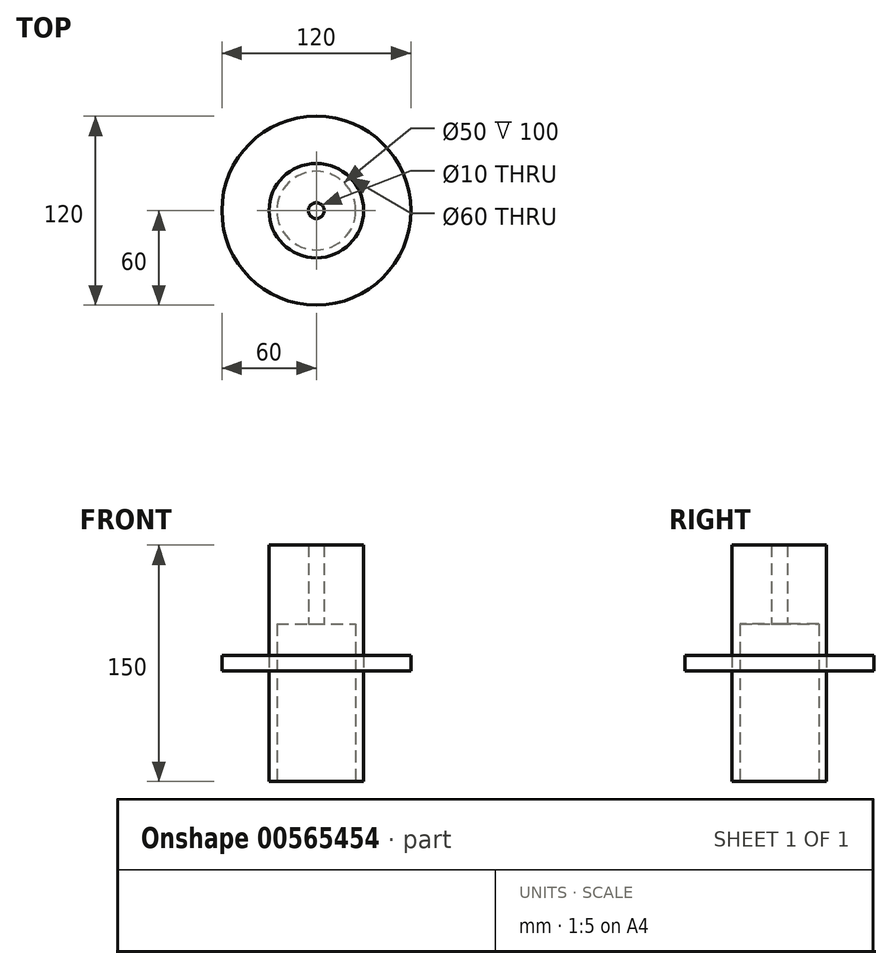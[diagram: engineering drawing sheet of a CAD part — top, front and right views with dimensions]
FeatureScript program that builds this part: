
annotation { "Feature Type Name" : "Feature", "Feature Type Description" : "" }
export const myFeature = defineFeature(function(context is Context, id is Id, definition is map)
    precondition{}
    {
        {
            var Q0;
            Q0=qCreatedBy(makeId("Top.planeOp"),FACE);
            var sketch = newSketch(context, id + "F0", { "sketchPlane" : qUnion([Q0])});
            skCircle(sketch, "E0", {"center": v(0, 0) * mm, "radius": 30 * mm});
            skSolve(sketch);
        }
        {
            var Q0;
            Q0 = qSketchRegion(id + "F0", true);
            extrude(context, id + "F1", {"entities" : qUnion([Q0]), "depth" : 150 * mm, "offsetDistance" : 25 * mm});
        }
        {
            var Q0;
            Q0=makeQuery(id+"F1.opExtrude","CAP_FACE",FACE,{"disambiguationData":[OSD([sQuery(id+"F0.wireOp",EDGE,"E0")])],"isStart":true});
            var sketch = newSketch(context, id + "F2", { "sketchPlane" : qUnion([Q0])});
            skCircle(sketch, "E1", {"center": v(0, 0) * mm, "radius": 25 * mm});
            skSolve(sketch);
        }
        {
            var Q0;
            Q0 = qSketchRegion(id + "F2", true);
            extrude(context, id + "F3", {"entities" : qUnion([Q0]), "operationType" : NewBodyOperationType.REMOVE, "oppositeDirection" : true, "depth" : 100 * mm, "offsetDistance" : 25 * mm});
        }
        {
            var Q0;
            Q0=qCreatedBy(makeId("Top.planeOp"),FACE);
            var sketch = newSketch(context, id + "F4", { "sketchPlane" : qUnion([Q0])});
            skCircle(sketch, "E2", {"center": v(0, 0) * mm, "radius": 5 * mm});
            skSolve(sketch);
        }
        {
            var Q0;
            Q0 = qSketchRegion(id + "F4", true);
            extrude(context, id + "F5", {"entities" : qUnion([Q0]), "operationType" : NewBodyOperationType.REMOVE, "endBound" : BoundingType.THROUGH_ALL, "depth" : 25 * mm, "offsetDistance" : 25 * mm});
        }
        {
            var Q0;
            Q0=qCreatedBy(makeId("Top.planeOp"),FACE);
            cPlane(context, id + "F6", {"entities" : qUnion([Q0]), "cplaneType" : CPlaneType.OFFSET, "offset" : 75 * mm, "width" : 150 * mm, "height" : 150 * mm});
        }
        {
            var Q0;
            Q0=qCreatedBy(id+"F6.planeOp",FACE);
            var sketch = newSketch(context, id + "F7", { "sketchPlane" : qUnion([Q0])});
            skCircle(sketch, "E3", {"center": v(0, 0) * mm, "radius": 60 * mm});
            skCircle(sketch, "E4", {"center": v(0, 0) * mm, "radius": 30 * mm});
            skSolve(sketch);
        }
        {
            var Q0;
            Q0 = qSketchRegion(id + "F7", true);
            extrude(context, id + "F8", {"entities" : qUnion([Q0]), "depth" : 5 * mm, "offsetDistance" : 25 * mm, "hasSecondDirection" : true, "secondDirectionOppositeDirection" : true, "secondDirectionDepth" : 5 * mm});
        }
    });
